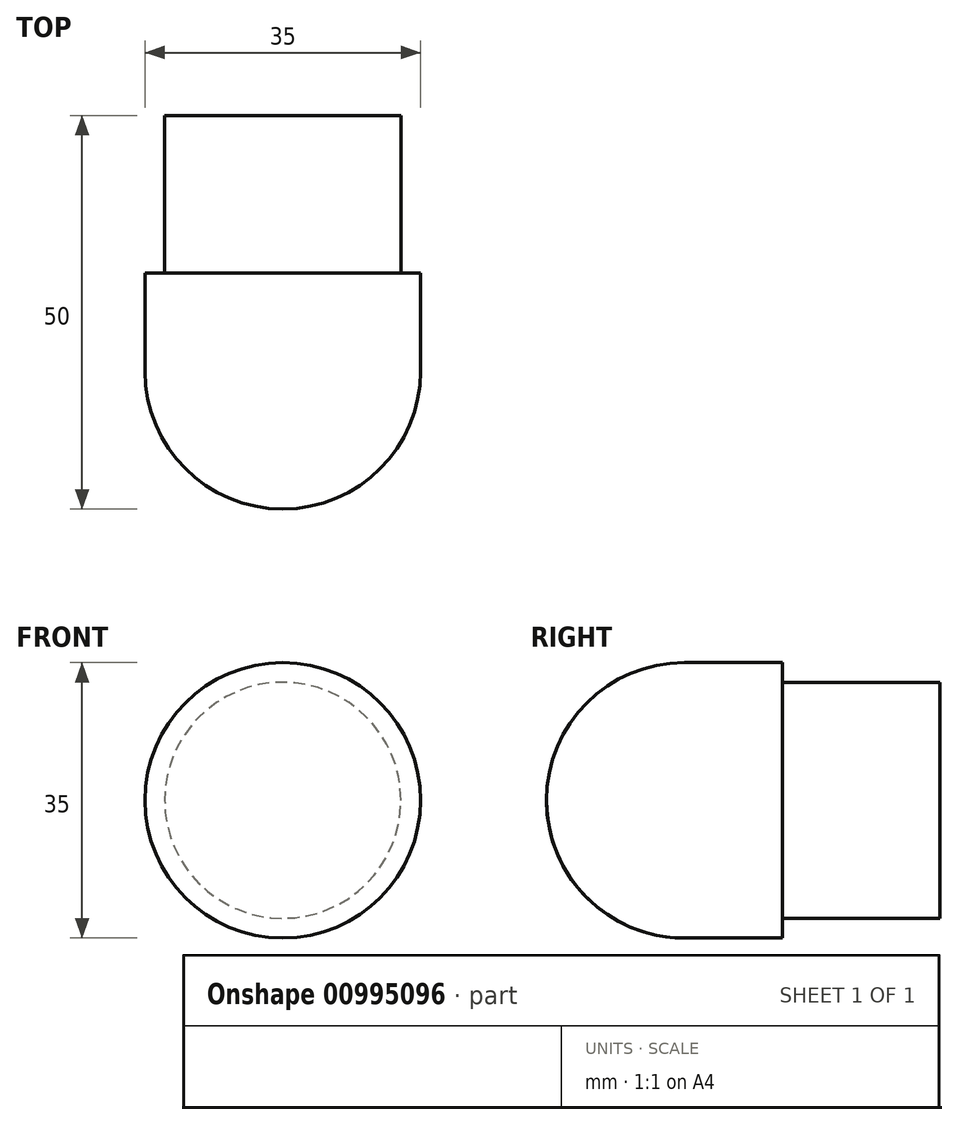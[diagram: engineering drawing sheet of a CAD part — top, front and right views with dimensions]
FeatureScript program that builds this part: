
annotation { "Feature Type Name" : "Feature", "Feature Type Description" : "" }
export const myFeature = defineFeature(function(context is Context, id is Id, definition is map)
    precondition{}
    {
        {
            var Q0;
            Q0=qCreatedBy(makeId("Front.planeOp"),FACE);
            var sketch = newSketch(context, id + "F0", { "sketchPlane" : qUnion([Q0])});
            skCircle(sketch, "E0", {"center": v(0, 0) * mm, "radius": 17.5 * mm});
            skCircle(sketch, "E1", {"center": v(0, 0) * mm, "radius": 15 * mm});
            skSolve(sketch);
        }
        {
            var Q0;
            Q0=makeQuery(id+"F0.imprint","IMPRINT",FACE,{"disambiguationData":[TD([[makeQuery(id+"F0.imprint","IMPRINT",EDGE,{"derivedFrom":sQuery(id+"F0.wireOp",EDGE,"E1")}),1.0]])]});
            var Q1;
            Q1=makeQuery(id+"F0.imprint","IMPRINT",FACE,{"disambiguationData":[TD([[makeQuery(id+"F0.imprint","IMPRINT",EDGE,{"derivedFrom":sQuery(id+"F0.wireOp",EDGE,"E0")}),1.0]])]});
            extrude(context, id + "F1", {"entities" : qUnion([Q0, Q1]), "depth" : 30 * mm, "offsetDistance" : 25 * mm});
        }
        {
            var Q0;
            Q0=makeQuery(id+"F0.imprint","IMPRINT",FACE,{"disambiguationData":[TD([[makeQuery(id+"F0.imprint","IMPRINT",EDGE,{"derivedFrom":sQuery(id+"F0.wireOp",EDGE,"E1")}),1.0]])]});
            extrude(context, id + "F2", {"entities" : qUnion([Q0]), "operationType" : NewBodyOperationType.ADD, "oppositeDirection" : true, "depth" : 20 * mm, "offsetDistance" : 25 * mm});
        }
        {
            var Q0;
            Q0=makeQuery(id+"F1.opExtrude","CAP_EDGE",EDGE,{"disambiguationData":[OSD([sQuery(id+"F0.wireOp",EDGE,"E0")])],"isStart":false});
            fillet(context, id + "F3", {"entities" : qUnion([Q0]), "radius" : 17.5 * mm, "tangentPropagation" : true, "allowEdgeOverflow" : false});
        }
    });
